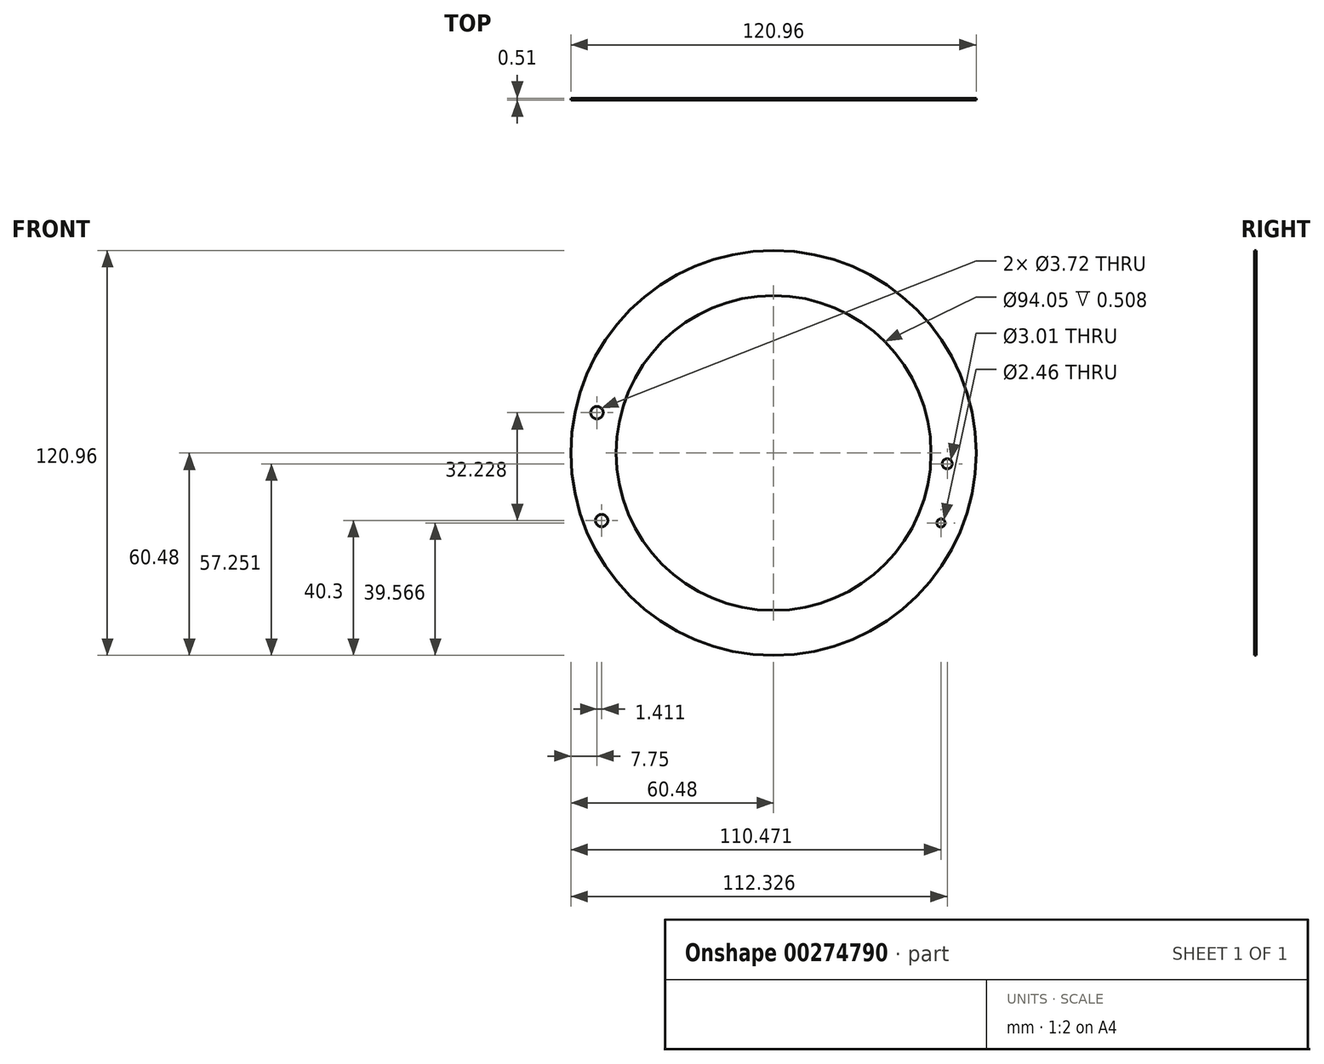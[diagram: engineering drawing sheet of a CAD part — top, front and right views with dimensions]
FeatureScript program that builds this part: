
annotation { "Feature Type Name" : "Feature", "Feature Type Description" : "" }
export const myFeature = defineFeature(function(context is Context, id is Id, definition is map)
    precondition{}
    {
        {
            var Q0;
            Q0=qCreatedBy(makeId("Front.planeOp"),FACE);
            var sketch = newSketch(context, id + "F0", { "sketchPlane" : qUnion([Q0])});
            skCircle(sketch, "E0", {"center": v(-51.32, -20.18) * mm, "radius": 1.86 * mm});
            skCircle(sketch, "E1", {"center": v(-52.73, 12.05) * mm, "radius": 1.86 * mm});
            skCircle(sketch, "E2", {"center": v(50, -20.91) * mm, "radius": 1.23 * mm});
            skCircle(sketch, "E3", {"center": v(51.85, -3.23) * mm, "radius": 1.5 * mm});
            skCircle(sketch, "E4", {"center": v(0, 0) * mm, "radius": 47.02 * mm});
            skCircle(sketch, "E5", {"center": v(0, 0) * mm, "radius": 60.48 * mm});
            skSolve(sketch);
        }
        {
            var Q0;
            Q0=makeQuery(id+"F0.imprint","IMPRINT",FACE,{"disambiguationData":[TD([[makeQuery(id+"F0.imprint","IMPRINT",EDGE,{"derivedFrom":sQuery(id+"F0.wireOp",EDGE,"E0")}),-1.0]])]});
            extrude(context, id + "F1", {"entities" : qUnion([Q0]), "depth" : 0.5 * mm});
        }
    });
